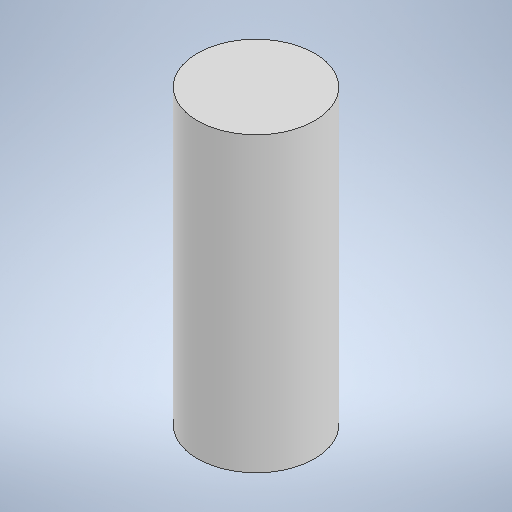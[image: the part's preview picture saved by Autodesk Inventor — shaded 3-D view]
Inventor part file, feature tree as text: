
AUTODESK INVENTOR PART (.ipt)
format: ipt  version: 2025.1 (Build 291241000, 241)  size: 213,504 bytes
history: native  units: mm
features: extrude x1, sketch x1
ambient origin geometry x8: Origin, YZ Plane, XZ Plane, XY Plane, X Axis, Y Axis, Z Axis, Center Point
bodies: Solid1 (feature_tree)
feature tree (2):
  extrude  "Extrusion1"  Depth=10.0mm TaperAngle=0.0deg
  sketch  "Sketch1"  dims[d0=4.0mm d1=10.0mm d2=0.0mm]
